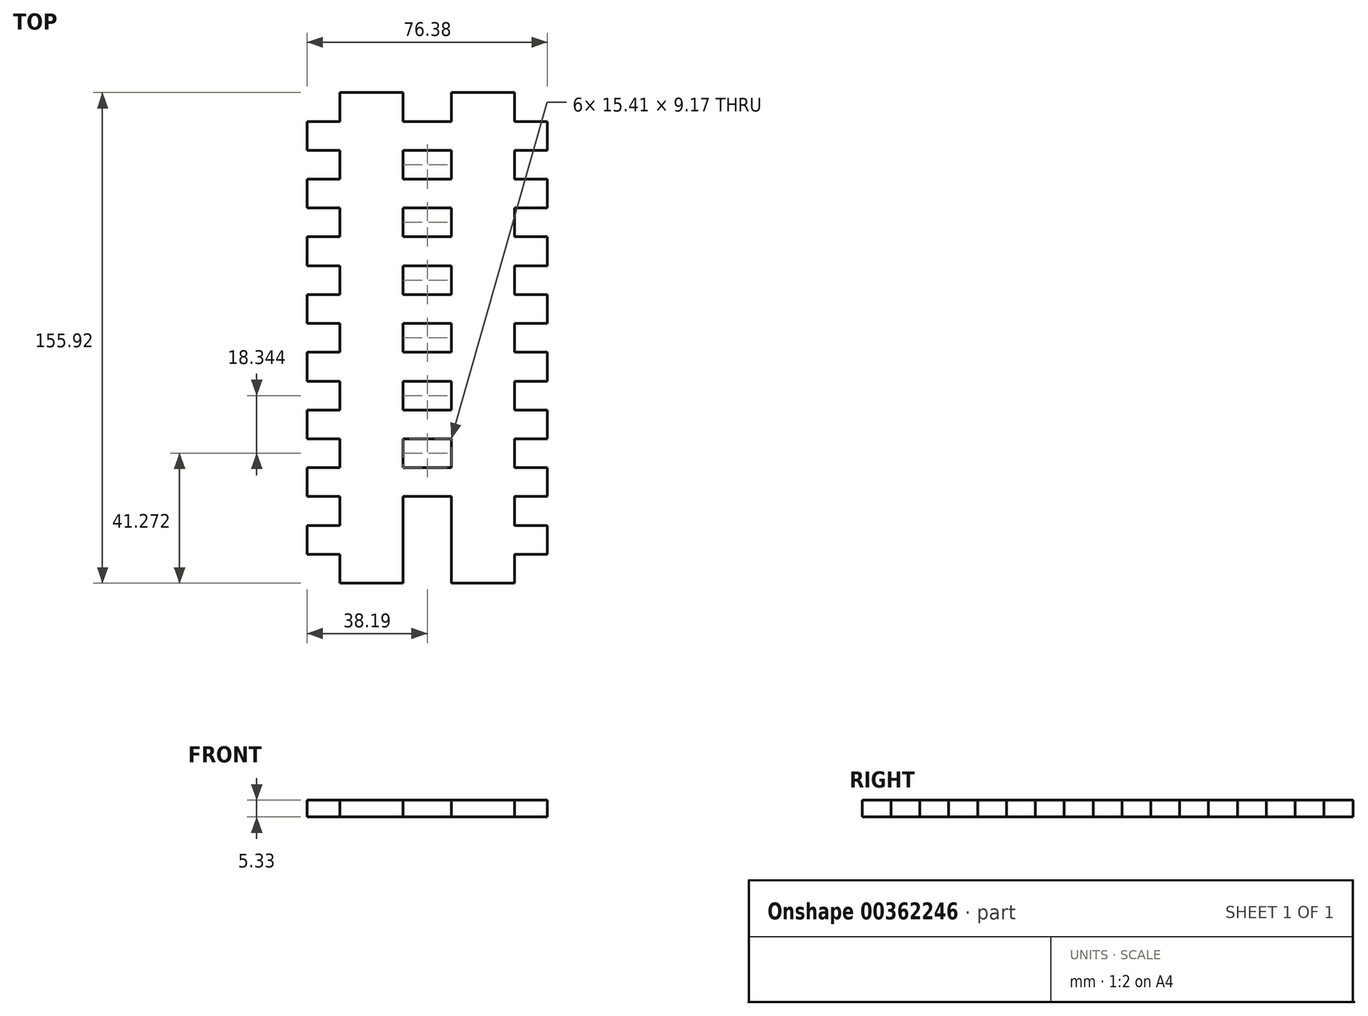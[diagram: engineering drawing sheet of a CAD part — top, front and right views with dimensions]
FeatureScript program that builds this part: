
annotation { "Feature Type Name" : "Feature", "Feature Type Description" : "" }
export const myFeature = defineFeature(function(context is Context, id is Id, definition is map)
    precondition{}
    {
        {
            var Q0;
            Q0=qCreatedBy(makeId("Top.planeOp"),FACE);
            var sketch = newSketch(context, id + "F0", { "sketchPlane" : qUnion([Q0])});
            skPoint(sketch, "E0.middle", {"position": v(0, 0) * mm});
            skLineSegment(sketch, "E1.top", {"start": v(7.7, -76.44) * mm, "end": v(27.74, -76.44) * mm});
            skLineSegment(sketch, "E2.bottom", {"start": v(-7.7, -76.44) * mm, "end": v(-27.74, -76.44) * mm});
            skLineSegment(sketch, "E3", {"start": v(-7.7, -76.44) * mm, "end": v(7.7, -76.44) * mm});
            skLineSegment(sketch, "E4", {"start": v(7.7, -67.27) * mm, "end": v(-7.7, -67.27) * mm});
            skLineSegment(sketch, "E5", {"start": v(-7.7, -67.27) * mm, "end": v(38.2, -67.27) * mm});
            skLineSegment(sketch, "E6", {"start": v(38.2, -67.27) * mm, "end": v(-38.2, -67.27) * mm});
            skLineSegment(sketch, "E7", {"start": v(27.74, -67.27) * mm, "end": v(27.74, -76.44) * mm});
            skLineSegment(sketch, "E8", {"start": v(38.2, -67.27) * mm, "end": v(38.2, -58.1) * mm});
            skLineSegment(sketch, "E9", {"start": v(38.2, -58.1) * mm, "end": v(38.2, -48.93) * mm});
            skLineSegment(sketch, "E10", {"start": v(38.2, -48.93) * mm, "end": v(38.2, -39.75) * mm});
            skLineSegment(sketch, "E11", {"start": v(38.2, -39.75) * mm, "end": v(38.2, -30.58) * mm});
            skLineSegment(sketch, "E12", {"start": v(38.2, -30.58) * mm, "end": v(38.2, -21.41) * mm});
            skLineSegment(sketch, "E13", {"start": v(-38.2, -67.27) * mm, "end": v(-38.2, -58.1) * mm});
            skLineSegment(sketch, "E14", {"start": v(38.2, -58.1) * mm, "end": v(-38.2, -58.1) * mm});
            skLineSegment(sketch, "E15", {"start": v(-27.74, -67.27) * mm, "end": v(-38.2, -67.27) * mm});
            skLineSegment(sketch, "E16", {"start": v(27.74, -67.27) * mm, "end": v(38.2, -67.27) * mm});
            skLineSegment(sketch, "E17", {"start": v(38.2, -48.93) * mm, "end": v(-38.2, -48.93) * mm});
            skLineSegment(sketch, "E18", {"start": v(38.2, -39.75) * mm, "end": v(-38.2, -39.75) * mm});
            skLineSegment(sketch, "E19", {"start": v(38.2, -30.58) * mm, "end": v(-38.2, -30.58) * mm});
            skLineSegment(sketch, "E20", {"start": v(38.2, -21.41) * mm, "end": v(38.2, -12.24) * mm});
            skLineSegment(sketch, "E21", {"start": v(38.2, -12.24) * mm, "end": v(38.2, -3.07) * mm});
            skLineSegment(sketch, "E22", {"start": v(38.2, -3.07) * mm, "end": v(38.2, 6.1) * mm});
            skLineSegment(sketch, "E23", {"start": v(38.2, 6.1) * mm, "end": v(38.2, 15.28) * mm});
            skLineSegment(sketch, "E24", {"start": v(38.2, 15.28) * mm, "end": v(38.2, 24.45) * mm});
            skLineSegment(sketch, "E25", {"start": v(38.2, 24.45) * mm, "end": v(38.2, 33.62) * mm});
            skLineSegment(sketch, "E26", {"start": v(38.2, 33.62) * mm, "end": v(38.2, 42.8) * mm});
            skLineSegment(sketch, "E27", {"start": v(38.2, 42.8) * mm, "end": v(38.2, 51.97) * mm});
            skLineSegment(sketch, "E28", {"start": v(38.2, 51.97) * mm, "end": v(38.2, 61.14) * mm});
            skLineSegment(sketch, "E29", {"start": v(38.2, 61.14) * mm, "end": v(38.2, 70.3) * mm});
            skLineSegment(sketch, "E30", {"start": v(38.2, 70.3) * mm, "end": v(38.2, 79.48) * mm});
            skLineSegment(sketch, "E31", {"start": v(38.2, -21.41) * mm, "end": v(-38.2, -21.41) * mm});
            skLineSegment(sketch, "E32", {"start": v(38.2, -12.24) * mm, "end": v(-38.2, -12.24) * mm});
            skLineSegment(sketch, "E33", {"start": v(38.2, -3.07) * mm, "end": v(-38.2, -3.07) * mm});
            skLineSegment(sketch, "E34", {"start": v(38.2, 6.1) * mm, "end": v(-38.2, 6.1) * mm});
            skLineSegment(sketch, "E35", {"start": v(38.2, 15.28) * mm, "end": v(-38.2, 15.28) * mm});
            skLineSegment(sketch, "E36", {"start": v(38.2, 24.45) * mm, "end": v(-38.2, 24.45) * mm});
            skLineSegment(sketch, "E37", {"start": v(38.2, 33.62) * mm, "end": v(-38.2, 33.62) * mm});
            skLineSegment(sketch, "E38", {"start": v(38.2, 42.8) * mm, "end": v(-38.2, 42.8) * mm});
            skLineSegment(sketch, "E39", {"start": v(38.2, 51.97) * mm, "end": v(-38.2, 51.97) * mm});
            skLineSegment(sketch, "E40", {"start": v(38.2, 61.14) * mm, "end": v(-38.2, 61.14) * mm});
            skLineSegment(sketch, "E41", {"start": v(38.2, 70.3) * mm, "end": v(-38.2, 70.3) * mm});
            skLineSegment(sketch, "E42", {"start": v(38.2, 79.48) * mm, "end": v(-38.2, 79.48) * mm});
            skLineSegment(sketch, "E43", {"start": v(27.74, -67.27) * mm, "end": v(27.74, 79.48) * mm});
            skLineSegment(sketch, "E44", {"start": v(-27.74, -76.44) * mm, "end": v(-27.74, 79.48) * mm});
            skLineSegment(sketch, "E45", {"start": v(7.7, -76.44) * mm, "end": v(7.7, 79.48) * mm});
            skLineSegment(sketch, "E46", {"start": v(-7.7, -76.44) * mm, "end": v(-7.7, 79.48) * mm});
            skLineSegment(sketch, "E47", {"start": v(-38.2, 79.48) * mm, "end": v(-38.2, 70.3) * mm});
            skLineSegment(sketch, "E48", {"start": v(-38.2, 70.3) * mm, "end": v(-38.2, 61.14) * mm});
            skLineSegment(sketch, "E49", {"start": v(-38.2, 51.97) * mm, "end": v(-38.2, 61.14) * mm});
            skLineSegment(sketch, "E50", {"start": v(-38.2, 51.97) * mm, "end": v(-38.2, 42.8) * mm});
            skLineSegment(sketch, "E51", {"start": v(-38.2, 42.8) * mm, "end": v(-38.2, 33.62) * mm});
            skLineSegment(sketch, "E52", {"start": v(-38.2, 33.62) * mm, "end": v(-38.2, 24.45) * mm});
            skLineSegment(sketch, "E53", {"start": v(-38.2, 24.45) * mm, "end": v(-38.2, 15.28) * mm});
            skLineSegment(sketch, "E54", {"start": v(-38.2, 15.28) * mm, "end": v(-38.2, 6.1) * mm});
            skLineSegment(sketch, "E55", {"start": v(-38.2, 6.1) * mm, "end": v(-38.2, -3.07) * mm});
            skLineSegment(sketch, "E56", {"start": v(-38.2, -3.07) * mm, "end": v(-38.2, -12.24) * mm});
            skLineSegment(sketch, "E57", {"start": v(-38.2, -12.24) * mm, "end": v(-38.2, -21.41) * mm});
            skLineSegment(sketch, "E58", {"start": v(-38.2, -21.41) * mm, "end": v(-38.2, -30.58) * mm});
            skLineSegment(sketch, "E59", {"start": v(-38.2, -30.58) * mm, "end": v(-38.2, -39.75) * mm});
            skLineSegment(sketch, "E60", {"start": v(-38.2, -39.75) * mm, "end": v(-38.2, -48.93) * mm});
            skLineSegment(sketch, "E61", {"start": v(-38.2, -48.93) * mm, "end": v(-38.2, -58.1) * mm});
            skSolve(sketch);
        }
        {
            var Q0;
            {var subQ0=sQuery(id+"F0.wireOp",EDGE,"E44");var subQ1=sQuery(id+"F0.wireOp",EDGE,"E41");var subQ2=makeQuery(id+"F0.imprint","INTERSECT",VERTEX,{"derivedFrom":[subQ1,subQ0]});Q0=makeQuery(id+"F0.imprint","IMPRINT",FACE,{"disambiguationData":[TD([[makeQuery(id+"F0.imprint","IMPRINT",EDGE,{"disambiguationData":[TD([[subQ2,1.0]])],"derivedFrom":subQ1}),-1.0]])]});}
            var Q1;
            {var subQ0=sQuery(id+"F0.wireOp",EDGE,"E44");var subQ1=sQuery(id+"F0.wireOp",EDGE,"E40");var subQ2=makeQuery(id+"F0.imprint","INTERSECT",VERTEX,{"derivedFrom":[subQ1,subQ0]});Q1=makeQuery(id+"F0.imprint","IMPRINT",FACE,{"disambiguationData":[TD([[makeQuery(id+"F0.imprint","IMPRINT",EDGE,{"disambiguationData":[TD([[subQ2,1.0]])],"derivedFrom":subQ1}),-1.0]])]});}
            var Q2;
            {var subQ0=sQuery(id+"F0.wireOp",EDGE,"E44");var subQ1=sQuery(id+"F0.wireOp",EDGE,"E38");var subQ2=makeQuery(id+"F0.imprint","INTERSECT",VERTEX,{"derivedFrom":[subQ1,subQ0]});Q2=makeQuery(id+"F0.imprint","IMPRINT",FACE,{"disambiguationData":[TD([[makeQuery(id+"F0.imprint","IMPRINT",EDGE,{"disambiguationData":[TD([[subQ2,1.0]])],"derivedFrom":subQ1}),-1.0]])]});}
            var Q3;
            {var subQ0=sQuery(id+"F0.wireOp",EDGE,"E44");var subQ1=sQuery(id+"F0.wireOp",EDGE,"E39");var subQ2=makeQuery(id+"F0.imprint","INTERSECT",VERTEX,{"derivedFrom":[subQ1,subQ0]});Q3=makeQuery(id+"F0.imprint","IMPRINT",FACE,{"disambiguationData":[TD([[makeQuery(id+"F0.imprint","IMPRINT",EDGE,{"disambiguationData":[TD([[subQ2,1.0]])],"derivedFrom":subQ1}),-1.0]])]});}
            var Q4;
            {var subQ0=sQuery(id+"F0.wireOp",EDGE,"E44");var subQ1=sQuery(id+"F0.wireOp",EDGE,"E37");var subQ2=makeQuery(id+"F0.imprint","INTERSECT",VERTEX,{"derivedFrom":[subQ1,subQ0]});Q4=makeQuery(id+"F0.imprint","IMPRINT",FACE,{"disambiguationData":[TD([[makeQuery(id+"F0.imprint","IMPRINT",EDGE,{"disambiguationData":[TD([[subQ2,1.0]])],"derivedFrom":subQ1}),-1.0]])]});}
            var Q5;
            {var subQ0=sQuery(id+"F0.wireOp",EDGE,"E44");var subQ1=sQuery(id+"F0.wireOp",EDGE,"E36");var subQ2=makeQuery(id+"F0.imprint","INTERSECT",VERTEX,{"derivedFrom":[subQ1,subQ0]});Q5=makeQuery(id+"F0.imprint","IMPRINT",FACE,{"disambiguationData":[TD([[makeQuery(id+"F0.imprint","IMPRINT",EDGE,{"disambiguationData":[TD([[subQ2,1.0]])],"derivedFrom":subQ1}),-1.0]])]});}
            var Q6;
            {var subQ0=sQuery(id+"F0.wireOp",EDGE,"E44");var subQ1=sQuery(id+"F0.wireOp",EDGE,"E31");var subQ2=makeQuery(id+"F0.imprint","INTERSECT",VERTEX,{"derivedFrom":[subQ1,subQ0]});Q6=makeQuery(id+"F0.imprint","IMPRINT",FACE,{"disambiguationData":[TD([[makeQuery(id+"F0.imprint","IMPRINT",EDGE,{"disambiguationData":[TD([[subQ2,1.0]])],"derivedFrom":subQ1}),-1.0]])]});}
            var Q7;
            {var subQ0=sQuery(id+"F0.wireOp",EDGE,"E44");var subQ1=sQuery(id+"F0.wireOp",EDGE,"E33");var subQ2=makeQuery(id+"F0.imprint","INTERSECT",VERTEX,{"derivedFrom":[subQ1,subQ0]});Q7=makeQuery(id+"F0.imprint","IMPRINT",FACE,{"disambiguationData":[TD([[makeQuery(id+"F0.imprint","IMPRINT",EDGE,{"disambiguationData":[TD([[subQ2,1.0]])],"derivedFrom":subQ1}),-1.0]])]});}
            var Q8;
            {var subQ0=sQuery(id+"F0.wireOp",EDGE,"E44");var subQ1=sQuery(id+"F0.wireOp",EDGE,"E18");var subQ2=makeQuery(id+"F0.imprint","INTERSECT",VERTEX,{"derivedFrom":[subQ1,subQ0]});Q8=makeQuery(id+"F0.imprint","IMPRINT",FACE,{"disambiguationData":[TD([[makeQuery(id+"F0.imprint","IMPRINT",EDGE,{"disambiguationData":[TD([[subQ2,1.0]])],"derivedFrom":subQ1}),-1.0]])]});}
            var Q9;
            {var subQ0=sQuery(id+"F0.wireOp",EDGE,"E44");var subQ1=sQuery(id+"F0.wireOp",EDGE,"E34");var subQ2=makeQuery(id+"F0.imprint","INTERSECT",VERTEX,{"derivedFrom":[subQ1,subQ0]});Q9=makeQuery(id+"F0.imprint","IMPRINT",FACE,{"disambiguationData":[TD([[makeQuery(id+"F0.imprint","IMPRINT",EDGE,{"disambiguationData":[TD([[subQ2,1.0]])],"derivedFrom":subQ1}),-1.0]])]});}
            var Q10;
            {var subQ0=sQuery(id+"F0.wireOp",EDGE,"E44");var subQ1=sQuery(id+"F0.wireOp",EDGE,"E32");var subQ2=makeQuery(id+"F0.imprint","INTERSECT",VERTEX,{"derivedFrom":[subQ1,subQ0]});Q10=makeQuery(id+"F0.imprint","IMPRINT",FACE,{"disambiguationData":[TD([[makeQuery(id+"F0.imprint","IMPRINT",EDGE,{"disambiguationData":[TD([[subQ2,1.0]])],"derivedFrom":subQ1}),-1.0]])]});}
            var Q11;
            {var subQ0=sQuery(id+"F0.wireOp",EDGE,"E44");var subQ1=sQuery(id+"F0.wireOp",EDGE,"E14");var subQ2=makeQuery(id+"F0.imprint","INTERSECT",VERTEX,{"derivedFrom":[subQ1,subQ0]});Q11=makeQuery(id+"F0.imprint","IMPRINT",FACE,{"disambiguationData":[TD([[makeQuery(id+"F0.imprint","IMPRINT",EDGE,{"disambiguationData":[TD([[subQ2,1.0]])],"derivedFrom":subQ1}),-1.0]])]});}
            var Q12;
            {var subQ0=sQuery(id+"F0.wireOp",EDGE,"E44");var subQ1=sQuery(id+"F0.wireOp",EDGE,"E19");var subQ2=makeQuery(id+"F0.imprint","INTERSECT",VERTEX,{"derivedFrom":[subQ1,subQ0]});Q12=makeQuery(id+"F0.imprint","IMPRINT",FACE,{"disambiguationData":[TD([[makeQuery(id+"F0.imprint","IMPRINT",EDGE,{"disambiguationData":[TD([[subQ2,1.0]])],"derivedFrom":subQ1}),-1.0]])]});}
            var Q13;
            {var subQ0=sQuery(id+"F0.wireOp",EDGE,"E44");var subQ1=sQuery(id+"F0.wireOp",EDGE,"E17");var subQ2=makeQuery(id+"F0.imprint","INTERSECT",VERTEX,{"derivedFrom":[subQ1,subQ0]});Q13=makeQuery(id+"F0.imprint","IMPRINT",FACE,{"disambiguationData":[TD([[makeQuery(id+"F0.imprint","IMPRINT",EDGE,{"disambiguationData":[TD([[subQ2,1.0]])],"derivedFrom":subQ1}),-1.0]])]});}
            var Q14;
            {var subQ0=sQuery(id+"F0.wireOp",EDGE,"E44");var subQ5=sQuery(id+"F0.wireOp",EDGE,"E14");var subQ6=makeQuery(id+"F0.imprint","INTERSECT",VERTEX,{"derivedFrom":[subQ5,subQ0]});Q14=makeQuery(id+"F0.imprint","IMPRINT",FACE,{"disambiguationData":[TD([[makeQuery(id+"F0.imprint","IMPRINT",EDGE,{"disambiguationData":[TD([[subQ6,1.0]])],"derivedFrom":subQ5}),1.0]])]});}
            var Q15;
            {var subQ0=sQuery(id+"F0.wireOp",EDGE,"E44");var subQ1=sQuery(id+"F0.wireOp",EDGE,"E35");var subQ2=makeQuery(id+"F0.imprint","INTERSECT",VERTEX,{"derivedFrom":[subQ1,subQ0]});Q15=makeQuery(id+"F0.imprint","IMPRINT",FACE,{"disambiguationData":[TD([[makeQuery(id+"F0.imprint","IMPRINT",EDGE,{"disambiguationData":[TD([[subQ2,1.0]])],"derivedFrom":subQ1}),-1.0]])]});}
            var Q16;
            {var subQ0=sQuery(id+"F0.wireOp",EDGE,"E43");var subQ1=sQuery(id+"F0.wireOp",EDGE,"E36");var subQ2=makeQuery(id+"F0.imprint","INTERSECT",VERTEX,{"derivedFrom":[subQ1,subQ0]});Q16=makeQuery(id+"F0.imprint","IMPRINT",FACE,{"disambiguationData":[TD([[makeQuery(id+"F0.imprint","IMPRINT",EDGE,{"disambiguationData":[TD([[subQ2,-1.0]])],"derivedFrom":subQ1}),-1.0]])]});}
            var Q17;
            {var subQ0=sQuery(id+"F0.wireOp",EDGE,"E43");var subQ1=sQuery(id+"F0.wireOp",EDGE,"E38");var subQ2=makeQuery(id+"F0.imprint","INTERSECT",VERTEX,{"derivedFrom":[subQ1,subQ0]});Q17=makeQuery(id+"F0.imprint","IMPRINT",FACE,{"disambiguationData":[TD([[makeQuery(id+"F0.imprint","IMPRINT",EDGE,{"disambiguationData":[TD([[subQ2,-1.0]])],"derivedFrom":subQ1}),-1.0]])]});}
            var Q18;
            {var subQ0=sQuery(id+"F0.wireOp",EDGE,"E43");var subQ5=sQuery(id+"F0.wireOp",EDGE,"E14");var subQ6=makeQuery(id+"F0.imprint","INTERSECT",VERTEX,{"derivedFrom":[subQ5,subQ0]});Q18=makeQuery(id+"F0.imprint","IMPRINT",FACE,{"disambiguationData":[TD([[makeQuery(id+"F0.imprint","IMPRINT",EDGE,{"disambiguationData":[TD([[subQ6,-1.0]])],"derivedFrom":subQ5}),1.0]])]});}
            var Q19;
            {var subQ0=sQuery(id+"F0.wireOp",EDGE,"E43");var subQ1=sQuery(id+"F0.wireOp",EDGE,"E35");var subQ2=makeQuery(id+"F0.imprint","INTERSECT",VERTEX,{"derivedFrom":[subQ1,subQ0]});Q19=makeQuery(id+"F0.imprint","IMPRINT",FACE,{"disambiguationData":[TD([[makeQuery(id+"F0.imprint","IMPRINT",EDGE,{"disambiguationData":[TD([[subQ2,-1.0]])],"derivedFrom":subQ1}),-1.0]])]});}
            var Q20;
            {var subQ0=sQuery(id+"F0.wireOp",EDGE,"E43");var subQ1=sQuery(id+"F0.wireOp",EDGE,"E14");var subQ2=makeQuery(id+"F0.imprint","INTERSECT",VERTEX,{"derivedFrom":[subQ1,subQ0]});Q20=makeQuery(id+"F0.imprint","IMPRINT",FACE,{"disambiguationData":[TD([[makeQuery(id+"F0.imprint","IMPRINT",EDGE,{"disambiguationData":[TD([[subQ2,-1.0]])],"derivedFrom":subQ1}),-1.0]])]});}
            var Q21;
            {var subQ0=sQuery(id+"F0.wireOp",EDGE,"E43");var subQ1=sQuery(id+"F0.wireOp",EDGE,"E19");var subQ2=makeQuery(id+"F0.imprint","INTERSECT",VERTEX,{"derivedFrom":[subQ1,subQ0]});Q21=makeQuery(id+"F0.imprint","IMPRINT",FACE,{"disambiguationData":[TD([[makeQuery(id+"F0.imprint","IMPRINT",EDGE,{"disambiguationData":[TD([[subQ2,-1.0]])],"derivedFrom":subQ1}),-1.0]])]});}
            var Q22;
            {var subQ0=sQuery(id+"F0.wireOp",EDGE,"E43");var subQ1=sQuery(id+"F0.wireOp",EDGE,"E32");var subQ2=makeQuery(id+"F0.imprint","INTERSECT",VERTEX,{"derivedFrom":[subQ1,subQ0]});Q22=makeQuery(id+"F0.imprint","IMPRINT",FACE,{"disambiguationData":[TD([[makeQuery(id+"F0.imprint","IMPRINT",EDGE,{"disambiguationData":[TD([[subQ2,-1.0]])],"derivedFrom":subQ1}),-1.0]])]});}
            var Q23;
            {var subQ0=sQuery(id+"F0.wireOp",EDGE,"E43");var subQ1=sQuery(id+"F0.wireOp",EDGE,"E37");var subQ2=makeQuery(id+"F0.imprint","INTERSECT",VERTEX,{"derivedFrom":[subQ1,subQ0]});Q23=makeQuery(id+"F0.imprint","IMPRINT",FACE,{"disambiguationData":[TD([[makeQuery(id+"F0.imprint","IMPRINT",EDGE,{"disambiguationData":[TD([[subQ2,-1.0]])],"derivedFrom":subQ1}),-1.0]])]});}
            var Q24;
            {var subQ0=sQuery(id+"F0.wireOp",EDGE,"E43");var subQ1=sQuery(id+"F0.wireOp",EDGE,"E18");var subQ2=makeQuery(id+"F0.imprint","INTERSECT",VERTEX,{"derivedFrom":[subQ1,subQ0]});Q24=makeQuery(id+"F0.imprint","IMPRINT",FACE,{"disambiguationData":[TD([[makeQuery(id+"F0.imprint","IMPRINT",EDGE,{"disambiguationData":[TD([[subQ2,-1.0]])],"derivedFrom":subQ1}),-1.0]])]});}
            var Q25;
            {var subQ0=sQuery(id+"F0.wireOp",EDGE,"E43");var subQ1=sQuery(id+"F0.wireOp",EDGE,"E34");var subQ2=makeQuery(id+"F0.imprint","INTERSECT",VERTEX,{"derivedFrom":[subQ1,subQ0]});Q25=makeQuery(id+"F0.imprint","IMPRINT",FACE,{"disambiguationData":[TD([[makeQuery(id+"F0.imprint","IMPRINT",EDGE,{"disambiguationData":[TD([[subQ2,-1.0]])],"derivedFrom":subQ1}),-1.0]])]});}
            var Q26;
            {var subQ0=sQuery(id+"F0.wireOp",EDGE,"E43");var subQ1=sQuery(id+"F0.wireOp",EDGE,"E17");var subQ2=makeQuery(id+"F0.imprint","INTERSECT",VERTEX,{"derivedFrom":[subQ1,subQ0]});Q26=makeQuery(id+"F0.imprint","IMPRINT",FACE,{"disambiguationData":[TD([[makeQuery(id+"F0.imprint","IMPRINT",EDGE,{"disambiguationData":[TD([[subQ2,-1.0]])],"derivedFrom":subQ1}),-1.0]])]});}
            var Q27;
            {var subQ0=sQuery(id+"F0.wireOp",EDGE,"E43");var subQ1=sQuery(id+"F0.wireOp",EDGE,"E40");var subQ2=makeQuery(id+"F0.imprint","INTERSECT",VERTEX,{"derivedFrom":[subQ1,subQ0]});Q27=makeQuery(id+"F0.imprint","IMPRINT",FACE,{"disambiguationData":[TD([[makeQuery(id+"F0.imprint","IMPRINT",EDGE,{"disambiguationData":[TD([[subQ2,-1.0]])],"derivedFrom":subQ1}),-1.0]])]});}
            var Q28;
            {var subQ0=sQuery(id+"F0.wireOp",EDGE,"E43");var subQ1=sQuery(id+"F0.wireOp",EDGE,"E41");var subQ2=makeQuery(id+"F0.imprint","INTERSECT",VERTEX,{"derivedFrom":[subQ1,subQ0]});Q28=makeQuery(id+"F0.imprint","IMPRINT",FACE,{"disambiguationData":[TD([[makeQuery(id+"F0.imprint","IMPRINT",EDGE,{"disambiguationData":[TD([[subQ2,-1.0]])],"derivedFrom":subQ1}),-1.0]])]});}
            var Q29;
            {var subQ0=sQuery(id+"F0.wireOp",EDGE,"E43");var subQ1=sQuery(id+"F0.wireOp",EDGE,"E39");var subQ2=makeQuery(id+"F0.imprint","INTERSECT",VERTEX,{"derivedFrom":[subQ1,subQ0]});Q29=makeQuery(id+"F0.imprint","IMPRINT",FACE,{"disambiguationData":[TD([[makeQuery(id+"F0.imprint","IMPRINT",EDGE,{"disambiguationData":[TD([[subQ2,-1.0]])],"derivedFrom":subQ1}),-1.0]])]});}
            var Q30;
            {var subQ0=sQuery(id+"F0.wireOp",EDGE,"E43");var subQ1=sQuery(id+"F0.wireOp",EDGE,"E31");var subQ2=makeQuery(id+"F0.imprint","INTERSECT",VERTEX,{"derivedFrom":[subQ1,subQ0]});Q30=makeQuery(id+"F0.imprint","IMPRINT",FACE,{"disambiguationData":[TD([[makeQuery(id+"F0.imprint","IMPRINT",EDGE,{"disambiguationData":[TD([[subQ2,-1.0]])],"derivedFrom":subQ1}),-1.0]])]});}
            var Q31;
            {var subQ0=sQuery(id+"F0.wireOp",EDGE,"E43");var subQ1=sQuery(id+"F0.wireOp",EDGE,"E33");var subQ2=makeQuery(id+"F0.imprint","INTERSECT",VERTEX,{"derivedFrom":[subQ1,subQ0]});Q31=makeQuery(id+"F0.imprint","IMPRINT",FACE,{"disambiguationData":[TD([[makeQuery(id+"F0.imprint","IMPRINT",EDGE,{"disambiguationData":[TD([[subQ2,-1.0]])],"derivedFrom":subQ1}),-1.0]])]});}
            var Q32;
            {var subQ0=sQuery(id+"F0.wireOp",EDGE,"E29");Q32=makeQuery(id+"F0.imprint","IMPRINT",FACE,{"disambiguationData":[TD([[makeQuery(id+"F0.imprint","IMPRINT",EDGE,{"derivedFrom":subQ0}),1.0]])]});}
            var Q33;
            {var subQ0=sQuery(id+"F0.wireOp",EDGE,"E45");var subQ1=sQuery(id+"F0.wireOp",EDGE,"E40");var subQ2=makeQuery(id+"F0.imprint","INTERSECT",VERTEX,{"derivedFrom":[subQ1,subQ0]});Q33=makeQuery(id+"F0.imprint","IMPRINT",FACE,{"disambiguationData":[TD([[makeQuery(id+"F0.imprint","IMPRINT",EDGE,{"disambiguationData":[TD([[subQ2,-1.0]])],"derivedFrom":subQ1}),-1.0]])]});}
            var Q34;
            {var subQ0=sQuery(id+"F0.wireOp",EDGE,"E48");Q34=makeQuery(id+"F0.imprint","IMPRINT",FACE,{"disambiguationData":[TD([[makeQuery(id+"F0.imprint","IMPRINT",EDGE,{"derivedFrom":subQ0}),1.0]])]});}
            var Q35;
            {var subQ0=sQuery(id+"F0.wireOp",EDGE,"E50");Q35=makeQuery(id+"F0.imprint","IMPRINT",FACE,{"disambiguationData":[TD([[makeQuery(id+"F0.imprint","IMPRINT",EDGE,{"derivedFrom":subQ0}),1.0]])]});}
            var Q36;
            {var subQ0=sQuery(id+"F0.wireOp",EDGE,"E45");var subQ1=sQuery(id+"F0.wireOp",EDGE,"E38");var subQ2=makeQuery(id+"F0.imprint","INTERSECT",VERTEX,{"derivedFrom":[subQ1,subQ0]});Q36=makeQuery(id+"F0.imprint","IMPRINT",FACE,{"disambiguationData":[TD([[makeQuery(id+"F0.imprint","IMPRINT",EDGE,{"disambiguationData":[TD([[subQ2,-1.0]])],"derivedFrom":subQ1}),-1.0]])]});}
            var Q37;
            {var subQ0=sQuery(id+"F0.wireOp",EDGE,"E27");Q37=makeQuery(id+"F0.imprint","IMPRINT",FACE,{"disambiguationData":[TD([[makeQuery(id+"F0.imprint","IMPRINT",EDGE,{"derivedFrom":subQ0}),1.0]])]});}
            var Q38;
            {var subQ0=sQuery(id+"F0.wireOp",EDGE,"E25");Q38=makeQuery(id+"F0.imprint","IMPRINT",FACE,{"disambiguationData":[TD([[makeQuery(id+"F0.imprint","IMPRINT",EDGE,{"derivedFrom":subQ0}),1.0]])]});}
            var Q39;
            {var subQ0=sQuery(id+"F0.wireOp",EDGE,"E45");var subQ1=sQuery(id+"F0.wireOp",EDGE,"E36");var subQ2=makeQuery(id+"F0.imprint","INTERSECT",VERTEX,{"derivedFrom":[subQ1,subQ0]});Q39=makeQuery(id+"F0.imprint","IMPRINT",FACE,{"disambiguationData":[TD([[makeQuery(id+"F0.imprint","IMPRINT",EDGE,{"disambiguationData":[TD([[subQ2,-1.0]])],"derivedFrom":subQ1}),-1.0]])]});}
            var Q40;
            {var subQ0=sQuery(id+"F0.wireOp",EDGE,"E52");Q40=makeQuery(id+"F0.imprint","IMPRINT",FACE,{"disambiguationData":[TD([[makeQuery(id+"F0.imprint","IMPRINT",EDGE,{"derivedFrom":subQ0}),1.0]])]});}
            var Q41;
            {var subQ0=sQuery(id+"F0.wireOp",EDGE,"E54");Q41=makeQuery(id+"F0.imprint","IMPRINT",FACE,{"disambiguationData":[TD([[makeQuery(id+"F0.imprint","IMPRINT",EDGE,{"derivedFrom":subQ0}),1.0]])]});}
            var Q42;
            {var subQ0=sQuery(id+"F0.wireOp",EDGE,"E23");Q42=makeQuery(id+"F0.imprint","IMPRINT",FACE,{"disambiguationData":[TD([[makeQuery(id+"F0.imprint","IMPRINT",EDGE,{"derivedFrom":subQ0}),1.0]])]});}
            var Q43;
            {var subQ0=sQuery(id+"F0.wireOp",EDGE,"E21");Q43=makeQuery(id+"F0.imprint","IMPRINT",FACE,{"disambiguationData":[TD([[makeQuery(id+"F0.imprint","IMPRINT",EDGE,{"derivedFrom":subQ0}),1.0]])]});}
            var Q44;
            {var subQ0=sQuery(id+"F0.wireOp",EDGE,"E56");Q44=makeQuery(id+"F0.imprint","IMPRINT",FACE,{"disambiguationData":[TD([[makeQuery(id+"F0.imprint","IMPRINT",EDGE,{"derivedFrom":subQ0}),1.0]])]});}
            var Q45;
            {var subQ0=sQuery(id+"F0.wireOp",EDGE,"E58");Q45=makeQuery(id+"F0.imprint","IMPRINT",FACE,{"disambiguationData":[TD([[makeQuery(id+"F0.imprint","IMPRINT",EDGE,{"derivedFrom":subQ0}),1.0]])]});}
            var Q46;
            {var subQ0=sQuery(id+"F0.wireOp",EDGE,"E45");var subQ1=sQuery(id+"F0.wireOp",EDGE,"E34");var subQ2=makeQuery(id+"F0.imprint","INTERSECT",VERTEX,{"derivedFrom":[subQ1,subQ0]});Q46=makeQuery(id+"F0.imprint","IMPRINT",FACE,{"disambiguationData":[TD([[makeQuery(id+"F0.imprint","IMPRINT",EDGE,{"disambiguationData":[TD([[subQ2,-1.0]])],"derivedFrom":subQ1}),-1.0]])]});}
            var Q47;
            {var subQ0=sQuery(id+"F0.wireOp",EDGE,"E45");var subQ1=sQuery(id+"F0.wireOp",EDGE,"E32");var subQ2=makeQuery(id+"F0.imprint","INTERSECT",VERTEX,{"derivedFrom":[subQ1,subQ0]});Q47=makeQuery(id+"F0.imprint","IMPRINT",FACE,{"disambiguationData":[TD([[makeQuery(id+"F0.imprint","IMPRINT",EDGE,{"disambiguationData":[TD([[subQ2,-1.0]])],"derivedFrom":subQ1}),-1.0]])]});}
            var Q48;
            {var subQ0=sQuery(id+"F0.wireOp",EDGE,"E45");var subQ1=sQuery(id+"F0.wireOp",EDGE,"E19");var subQ2=makeQuery(id+"F0.imprint","INTERSECT",VERTEX,{"derivedFrom":[subQ1,subQ0]});Q48=makeQuery(id+"F0.imprint","IMPRINT",FACE,{"disambiguationData":[TD([[makeQuery(id+"F0.imprint","IMPRINT",EDGE,{"disambiguationData":[TD([[subQ2,-1.0]])],"derivedFrom":subQ1}),-1.0]])]});}
            var Q49;
            {var subQ0=sQuery(id+"F0.wireOp",EDGE,"E45");var subQ1=sQuery(id+"F0.wireOp",EDGE,"E17");var subQ2=makeQuery(id+"F0.imprint","INTERSECT",VERTEX,{"derivedFrom":[subQ1,subQ0]});Q49=makeQuery(id+"F0.imprint","IMPRINT",FACE,{"disambiguationData":[TD([[makeQuery(id+"F0.imprint","IMPRINT",EDGE,{"disambiguationData":[TD([[subQ2,-1.0]])],"derivedFrom":subQ1}),-1.0]])]});}
            var Q50;
            {var subQ0=sQuery(id+"F0.wireOp",EDGE,"E12");Q50=makeQuery(id+"F0.imprint","IMPRINT",FACE,{"disambiguationData":[TD([[makeQuery(id+"F0.imprint","IMPRINT",EDGE,{"derivedFrom":subQ0}),1.0]])]});}
            var Q51;
            {var subQ0=sQuery(id+"F0.wireOp",EDGE,"E10");Q51=makeQuery(id+"F0.imprint","IMPRINT",FACE,{"disambiguationData":[TD([[makeQuery(id+"F0.imprint","IMPRINT",EDGE,{"derivedFrom":subQ0}),1.0]])]});}
            var Q52;
            {var subQ0=sQuery(id+"F0.wireOp",EDGE,"E60");Q52=makeQuery(id+"F0.imprint","IMPRINT",FACE,{"disambiguationData":[TD([[makeQuery(id+"F0.imprint","IMPRINT",EDGE,{"derivedFrom":subQ0}),1.0]])]});}
            var Q53;
            {var subQ0=sQuery(id+"F0.wireOp",EDGE,"E13");Q53=makeQuery(id+"F0.imprint","IMPRINT",FACE,{"disambiguationData":[TD([[makeQuery(id+"F0.imprint","IMPRINT",EDGE,{"derivedFrom":subQ0}),-1.0]])]});}
            var Q54;
            {var subQ0=sQuery(id+"F0.wireOp",EDGE,"E45");var subQ1=sQuery(id+"F0.wireOp",EDGE,"E6");var subQ2=makeQuery(id+"F0.imprint","INTERSECT",VERTEX,{"derivedFrom":[subQ1,subQ0]});Q54=makeQuery(id+"F0.imprint","IMPRINT",FACE,{"disambiguationData":[TD([[makeQuery(id+"F0.imprint","IMPRINT",EDGE,{"disambiguationData":[TD([[subQ2,-1.0]])],"derivedFrom":subQ1}),-1.0]])]});}
            var Q55;
            {var subQ0=sQuery(id+"F0.wireOp",EDGE,"E8");Q55=makeQuery(id+"F0.imprint","IMPRINT",FACE,{"disambiguationData":[TD([[makeQuery(id+"F0.imprint","IMPRINT",EDGE,{"derivedFrom":subQ0}),1.0]])]});}
            var Q56;
            {var subQ0=sQuery(id+"F0.wireOp",EDGE,"E2.bottom");Q56=makeQuery(id+"F0.imprint","IMPRINT",FACE,{"disambiguationData":[TD([[makeQuery(id+"F0.imprint","IMPRINT",EDGE,{"derivedFrom":subQ0}),-1.0]])]});}
            var Q57;
            {var subQ0=sQuery(id+"F0.wireOp",EDGE,"E1.top");Q57=makeQuery(id+"F0.imprint","IMPRINT",FACE,{"disambiguationData":[TD([[makeQuery(id+"F0.imprint","IMPRINT",EDGE,{"derivedFrom":subQ0}),1.0]])]});}
            extrude(context, id + "F1", {"entities" : qUnion([Q0, Q1, Q2, Q3, Q4, Q5, Q6, Q7, Q8, Q9, Q10, Q11, Q12, Q13, Q14, Q15, Q16, Q17, Q18, Q19, Q20, Q21, Q22, Q23, Q24, Q25, Q26, Q27, Q28, Q29, Q30, Q31, Q32, Q33, Q34, Q35, Q36, Q37, Q38, Q39, Q40, Q41, Q42, Q43, Q44, Q45, Q46, Q47, Q48, Q49, Q50, Q51, Q52, Q53, Q54, Q55, Q56, Q57]), "depth" : 5.33 * mm});
        }
    });
